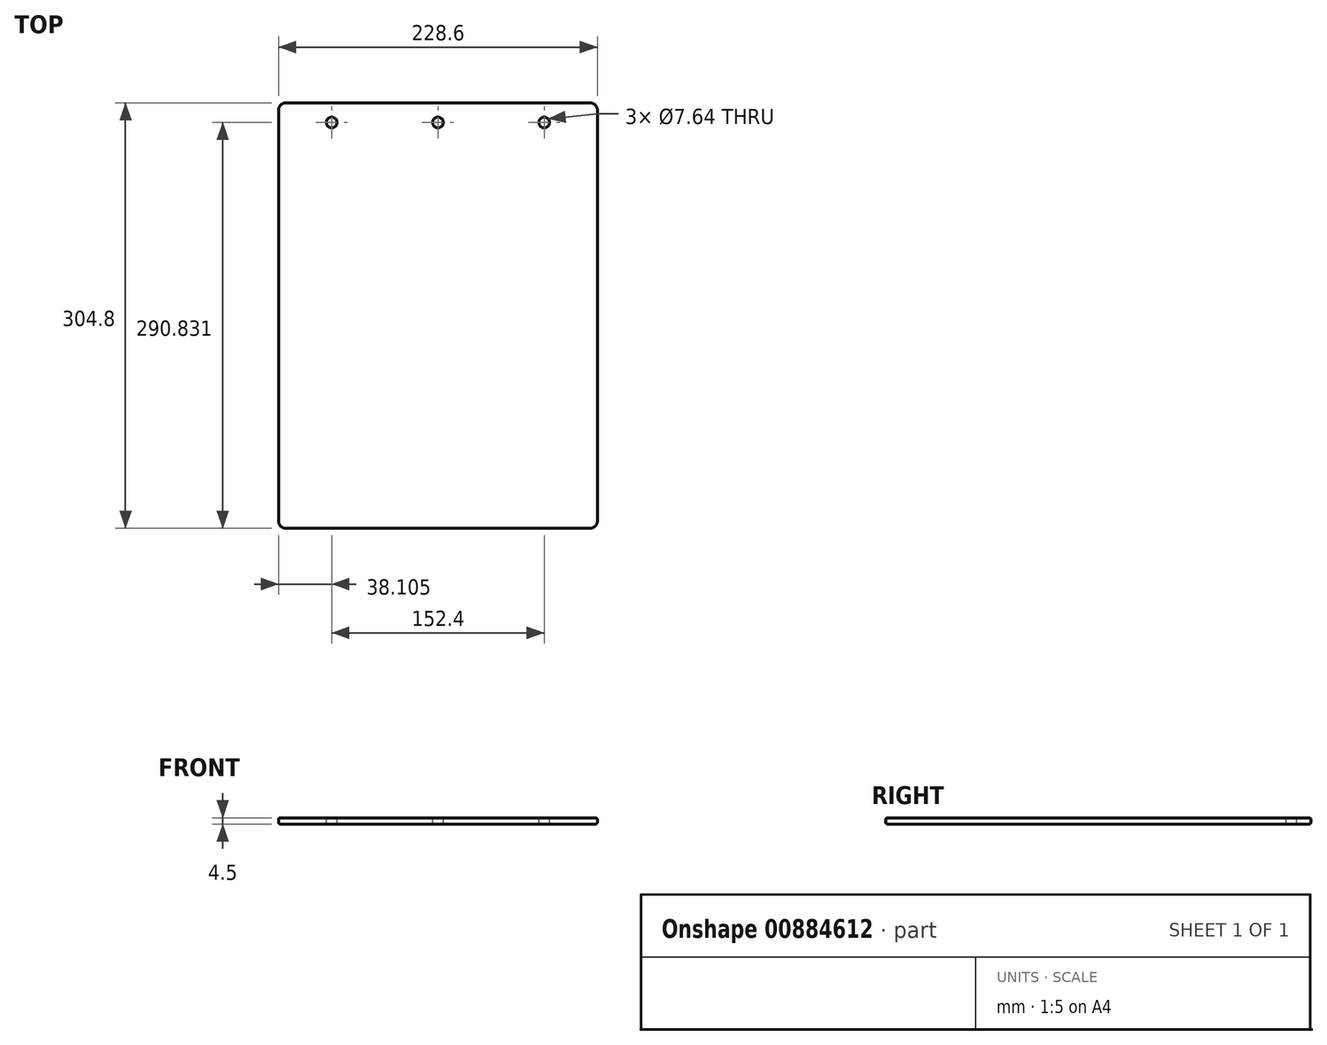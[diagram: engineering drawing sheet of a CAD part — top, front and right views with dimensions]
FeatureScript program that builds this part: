
annotation { "Feature Type Name" : "Feature", "Feature Type Description" : "" }
export const myFeature = defineFeature(function(context is Context, id is Id, definition is map)
    precondition{}
    {
        {
            var Q0;
            Q0=qCreatedBy(makeId("Top.planeOp"),FACE);
            var sketch = newSketch(context, id + "F0", { "sketchPlane" : qUnion([Q0])});
            skLineSegment(sketch, "E0.bottom", {"start": v(-36.25, 253.94) * mm, "end": v(192.35, 253.94) * mm});
            skLineSegment(sketch, "E0.top", {"start": v(-36.25, -50.86) * mm, "end": v(192.35, -50.86) * mm});
            skLineSegment(sketch, "E0.left", {"start": v(-36.25, 253.94) * mm, "end": v(-36.25, -50.86) * mm});
            skLineSegment(sketch, "E0.right", {"start": v(192.35, 253.94) * mm, "end": v(192.35, -50.86) * mm});
            skSolve(sketch);
        }
        {
            var Q0;
            Q0=makeQuery(id+"F0.imprint","IMPRINT",FACE,{"disambiguationData":[TD([[makeQuery(id+"F0.imprint","IMPRINT",EDGE,{"derivedFrom":sQuery(id+"F0.wireOp",EDGE,"E0.bottom")}),-1.0]])]});
            extrude(context, id + "F1", {"entities" : qUnion([Q0]), "depth" : 4.5 * mm, "offsetDistance" : 25.4 * mm});
        }
        {
            var Q0;
            Q0=makeQuery(id+"F1.opExtrude","SWEPT_EDGE",EDGE,{"disambiguationData":[OSD([sQuery(id+"F0.wireOp",EDGE,"E0.bottom"),sQuery(id+"F0.wireOp",EDGE,"E0.left")])]});
            var Q1;
            Q1=makeQuery(id+"F1.opExtrude","SWEPT_EDGE",EDGE,{"disambiguationData":[OSD([sQuery(id+"F0.wireOp",EDGE,"E0.bottom"),sQuery(id+"F0.wireOp",EDGE,"E0.right")])]});
            var Q2;
            Q2=makeQuery(id+"F1.opExtrude","SWEPT_EDGE",EDGE,{"disambiguationData":[OSD([sQuery(id+"F0.wireOp",EDGE,"E0.top"),sQuery(id+"F0.wireOp",EDGE,"E0.left")])]});
            var Q3;
            Q3=makeQuery(id+"F1.opExtrude","SWEPT_EDGE",EDGE,{"disambiguationData":[OSD([sQuery(id+"F0.wireOp",EDGE,"E0.top"),sQuery(id+"F0.wireOp",EDGE,"E0.right")])]});
            fillet(context, id + "F2", {"entities" : qUnion([Q0, Q1, Q2, Q3]), "radius" : 5.08 * mm, "tangentPropagation" : true, "allowEdgeOverflow" : false});
        }
        {
            var Q0;
            Q0=makeQuery(id+"F1.opExtrude","SWEPT_FACE",FACE,{"disambiguationData":[OSD([sQuery(id+"F0.wireOp",EDGE,"E0.top")])]});
            fillet(context, id + "F3", {"entities" : qUnion([Q0]), "radius" : 1.27 * mm, "tangentPropagation" : true, "allowEdgeOverflow" : false});
        }
        {
            var Q0;
            Q0=makeQuery(id+"F1.opExtrude","CAP_FACE",FACE,{"disambiguationData":[OSD([sQuery(id+"F0.wireOp",EDGE,"E0.bottom"),sQuery(id+"F0.wireOp",EDGE,"E0.top"),sQuery(id+"F0.wireOp",EDGE,"E0.left"),sQuery(id+"F0.wireOp",EDGE,"E0.right")])],"isStart":false});
            var sketch = newSketch(context, id + "F4", { "sketchPlane" : qUnion([Q0])});
            skCircle(sketch, "E1", {"center": v(1.85, 239.97) * mm, "radius": 3.82 * mm});
            skCircle(sketch, "E2", {"center": v(78.05, 239.97) * mm, "radius": 3.82 * mm});
            skCircle(sketch, "E3", {"center": v(154.25, 239.97) * mm, "radius": 3.82 * mm});
            skSolve(sketch);
        }
        {
            var Q0;
            Q0=makeQuery(id+"F4.imprint","IMPRINT",FACE,{"disambiguationData":[TD([[makeQuery(id+"F4.imprint","IMPRINT",EDGE,{"derivedFrom":sQuery(id+"F4.wireOp",EDGE,"E1")}),1.0]])]});
            var Q1;
            Q1=makeQuery(id+"F4.imprint","IMPRINT",FACE,{"disambiguationData":[TD([[makeQuery(id+"F4.imprint","IMPRINT",EDGE,{"derivedFrom":sQuery(id+"F4.wireOp",EDGE,"E2")}),1.0]])]});
            var Q2;
            Q2=makeQuery(id+"F4.imprint","IMPRINT",FACE,{"disambiguationData":[TD([[makeQuery(id+"F4.imprint","IMPRINT",EDGE,{"derivedFrom":sQuery(id+"F4.wireOp",EDGE,"E3")}),1.0]])]});
            extrude(context, id + "F5", {"entities" : qUnion([Q0, Q1, Q2]), "operationType" : NewBodyOperationType.REMOVE, "oppositeDirection" : true, "depth" : 4.5 * mm, "offsetDistance" : 25.4 * mm});
        }
    });
